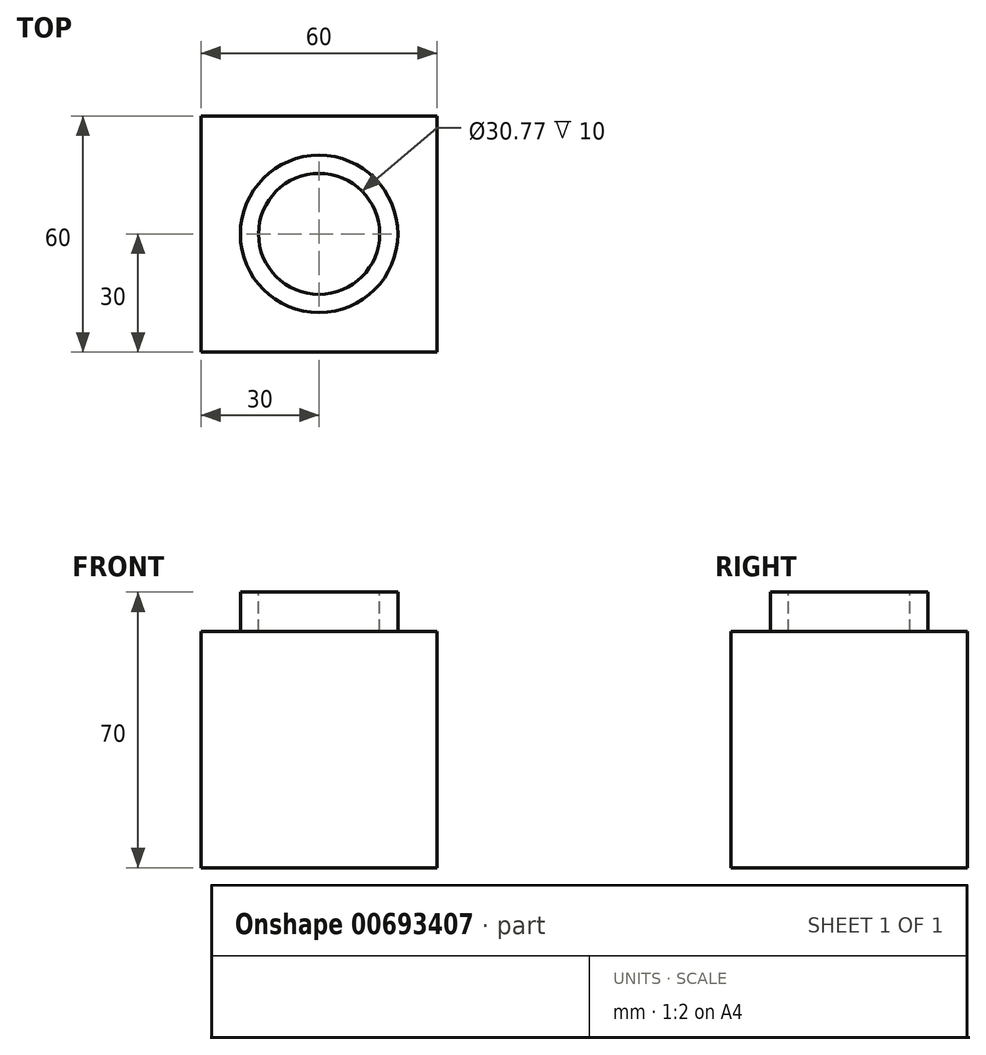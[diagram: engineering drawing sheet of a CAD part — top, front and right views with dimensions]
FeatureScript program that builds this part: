
annotation { "Feature Type Name" : "Feature", "Feature Type Description" : "" }
export const myFeature = defineFeature(function(context is Context, id is Id, definition is map)
    precondition{}
    {
        {
            var Q0;
            Q0=qCreatedBy(makeId("Top.planeOp"),FACE);
            var sketch = newSketch(context, id + "F0", { "sketchPlane" : qUnion([Q0])});
            skLineSegment(sketch, "E0.bottom", {"start": v(30, 30) * mm, "end": v(-30, 30) * mm});
            skLineSegment(sketch, "E0.top", {"start": v(30, -30) * mm, "end": v(-30, -30) * mm});
            skLineSegment(sketch, "E0.left", {"start": v(30, 30) * mm, "end": v(30, -30) * mm});
            skLineSegment(sketch, "E0.right", {"start": v(-30, 30) * mm, "end": v(-30, -30) * mm});
            skPoint(sketch, "E0.middle", {"position": v(0, 0) * mm});
            skSolve(sketch);
        }
        {
            var Q0;
            Q0=makeQuery(id+"F0.imprint","IMPRINT",FACE,{"disambiguationData":[TD([[makeQuery(id+"F0.imprint","IMPRINT",EDGE,{"derivedFrom":sQuery(id+"F0.wireOp",EDGE,"E0.bottom")}),1.0]])]});
            extrude(context, id + "F1", {"entities" : qUnion([Q0]), "depth" : 30 * mm, "offsetDistance" : 25 * mm});
        }
        {
            var Q0;
            Q0=makeQuery(id+"F1.opExtrude","CAP_FACE",FACE,{"disambiguationData":[OSD([sQuery(id+"F0.wireOp",EDGE,"E0.bottom"),sQuery(id+"F0.wireOp",EDGE,"E0.top"),sQuery(id+"F0.wireOp",EDGE,"E0.left"),sQuery(id+"F0.wireOp",EDGE,"E0.right")])],"isStart":true});
            extrude(context, id + "F2", {"entities" : qUnion([Q0]), "operationType" : NewBodyOperationType.ADD, "depth" : 30 * mm, "offsetDistance" : 25 * mm});
        }
        {
            var Q0;
            Q0=makeQuery(id+"F1.opExtrude","CAP_FACE",FACE,{"disambiguationData":[OSD([sQuery(id+"F0.wireOp",EDGE,"E0.bottom"),sQuery(id+"F0.wireOp",EDGE,"E0.top"),sQuery(id+"F0.wireOp",EDGE,"E0.left"),sQuery(id+"F0.wireOp",EDGE,"E0.right")])],"isStart":false});
            var sketch = newSketch(context, id + "F3", { "sketchPlane" : qUnion([Q0])});
            skCircle(sketch, "E1", {"center": v(0, 0) * mm, "radius": 20 * mm});
            skSolve(sketch);
        }
        {
            var Q0;
            {var subQ0=sQuery(id+"F3.wireOp",EDGE,"E1");var subQ1=makeQuery(id+"F3.imprint","INTERSECT",VERTEX,{"derivedFrom":[makeQuery(id+"F1.opExtrude","CAP_EDGE",EDGE,{"disambiguationData":[OSD([sQuery(id+"F0.wireOp",EDGE,"E0.bottom")])],"isStart":false}),subQ0]});Q0=makeQuery(id+"F3.imprint","IMPRINT",FACE,{"disambiguationData":[TD([[makeQuery(id+"F3.imprint","IMPRINT",EDGE,{"disambiguationData":[TD([[subQ1,1.0]])],"derivedFrom":subQ0}),1.0]])]});}
            extrude(context, id + "F4", {"entities" : qUnion([Q0]), "operationType" : NewBodyOperationType.ADD, "depth" : 10 * mm, "offsetDistance" : 25 * mm});
        }
        {
            var Q0;
            Q0=makeQuery(id+"F4.opExtrude","CAP_FACE",FACE,{"disambiguationData":[OSD([sQuery(id+"F3.wireOp",EDGE,"E1")])],"isStart":false});
            var sketch = newSketch(context, id + "F5", { "sketchPlane" : qUnion([Q0])});
            skSolve(sketch);
        }
        {
            var Q0;
            Q0=makeQuery(id+"F5.imprint","IMPRINT",FACE,{"disambiguationData":[TD([[makeQuery(id+"F5.imprint","IMPRINT",EDGE,{"derivedFrom":makeQuery(id+"F4.opExtrude","CAP_EDGE",EDGE,{"disambiguationData":[OSD([sQuery(id+"F3.wireOp",EDGE,"E1")])],"isStart":false})}),1.0]])]});
            var sketch = newSketch(context, id + "F6", { "sketchPlane" : qUnion([Q0])});
            skCircle(sketch, "E2", {"center": v(0, 0) * mm, "radius": 15.38 * mm});
            skSolve(sketch);
        }
        {
            var Q0;
            Q0=makeQuery(id+"F6.imprint","IMPRINT",FACE,{"disambiguationData":[TD([[makeQuery(id+"F6.imprint","IMPRINT",EDGE,{"derivedFrom":sQuery(id+"F6.wireOp",EDGE,"E2")}),1.0]])]});
            extrude(context, id + "F7", {"entities" : qUnion([Q0]), "operationType" : NewBodyOperationType.REMOVE, "oppositeDirection" : true, "depth" : 10 * mm, "offsetDistance" : 25 * mm});
        }
        {
            var Q0;
            {var subQ0=sQuery(id+"F0.wireOp",EDGE,"E0.bottom");Q0=makeQuery(id+"F2.boolean.opBoolean","MERGE",FACE,{"derivedFrom":[makeQuery(id+"F1.opExtrude","SWEPT_FACE",FACE,{"disambiguationData":[OSD([subQ0])]}),makeQuery(id+"F2.opExtrude","SWEPT_FACE",FACE,{"disambiguationData":[OSD([subQ0])]})]});}
            var sketch = newSketch(context, id + "F8", { "sketchPlane" : qUnion([Q0])});
            skSolve(sketch);
        }
        {
            var Q0;
            {var subQ0=sQuery(id+"F0.wireOp",EDGE,"E0.bottom");Q0=makeQuery(id+"F8.imprint","IMPRINT",FACE,{"disambiguationData":[TD([[makeQuery(id+"F8.imprint","IMPRINT",EDGE,{"derivedFrom":makeQuery(id+"F1.opExtrude","CAP_EDGE",EDGE,{"disambiguationData":[OSD([subQ0])],"isStart":false})}),-1.0]])]});}
            extrude(context, id + "F9", {"entities" : qUnion([Q0]), "operationType" : NewBodyOperationType.REMOVE, "depth" : 4 * mm, "offsetDistance" : 25 * mm});
        }
    });
